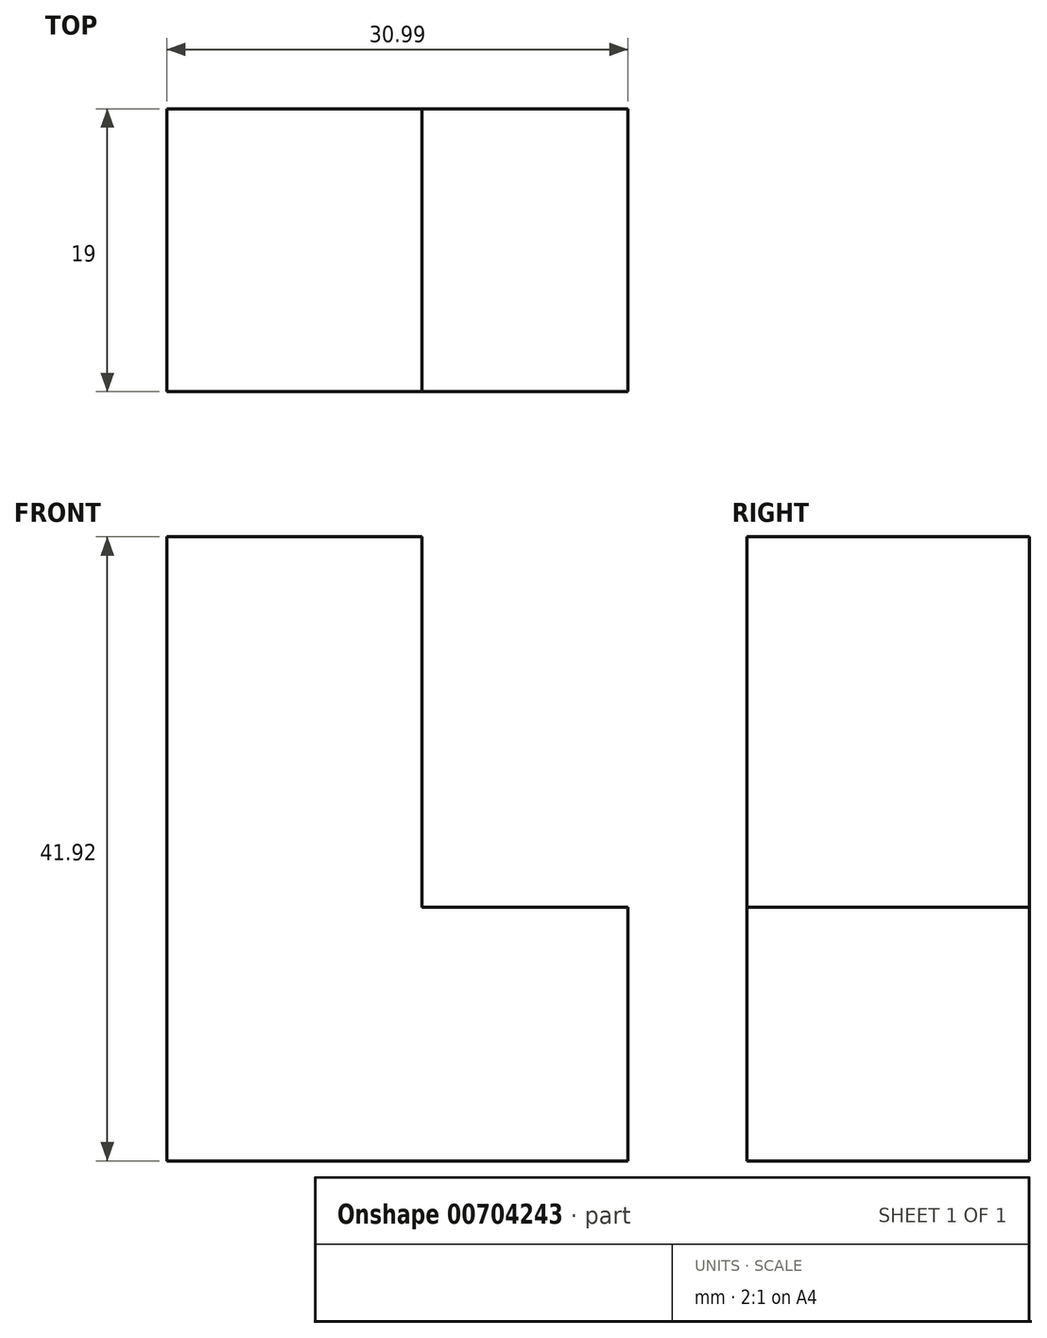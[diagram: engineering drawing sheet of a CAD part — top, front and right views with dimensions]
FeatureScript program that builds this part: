
annotation { "Feature Type Name" : "Feature", "Feature Type Description" : "" }
export const myFeature = defineFeature(function(context is Context, id is Id, definition is map)
    precondition{}
    {
        {
            var Q0;
            Q0=qCreatedBy(makeId("Front.planeOp"),FACE);
            var sketch = newSketch(context, id + "F0", { "sketchPlane" : qUnion([Q0])});
            skLineSegment(sketch, "E0", {"start": v(0, 0) * mm, "end": v(0, 24.88) * mm});
            skLineSegment(sketch, "E1", {"start": v(-17.14, 24.88) * mm, "end": v(0, 24.88) * mm});
            skLineSegment(sketch, "E2", {"start": v(-17.14, 24.88) * mm, "end": v(-17.14, -17.04) * mm});
            skLineSegment(sketch, "E3", {"start": v(13.85, 0) * mm, "end": v(13.85, -17.04) * mm});
            skLineSegment(sketch, "E4", {"start": v(13.85, -17.04) * mm, "end": v(-17.14, -17.04) * mm});
            skLineSegment(sketch, "E5", {"start": v(1.28, 0) * mm, "end": v(0, 0) * mm});
            skLineSegment(sketch, "E6", {"start": v(0, 0) * mm, "end": v(13.85, 0) * mm});
            skSolve(sketch);
        }
        {
            var Q0;
            Q0 = qSketchRegion(id + "F0", true);
            extrude(context, id + "F1", {"entities" : qUnion([Q0]), "depth" : 19 * mm, "offsetDistance" : 25 * mm});
        }
    });
